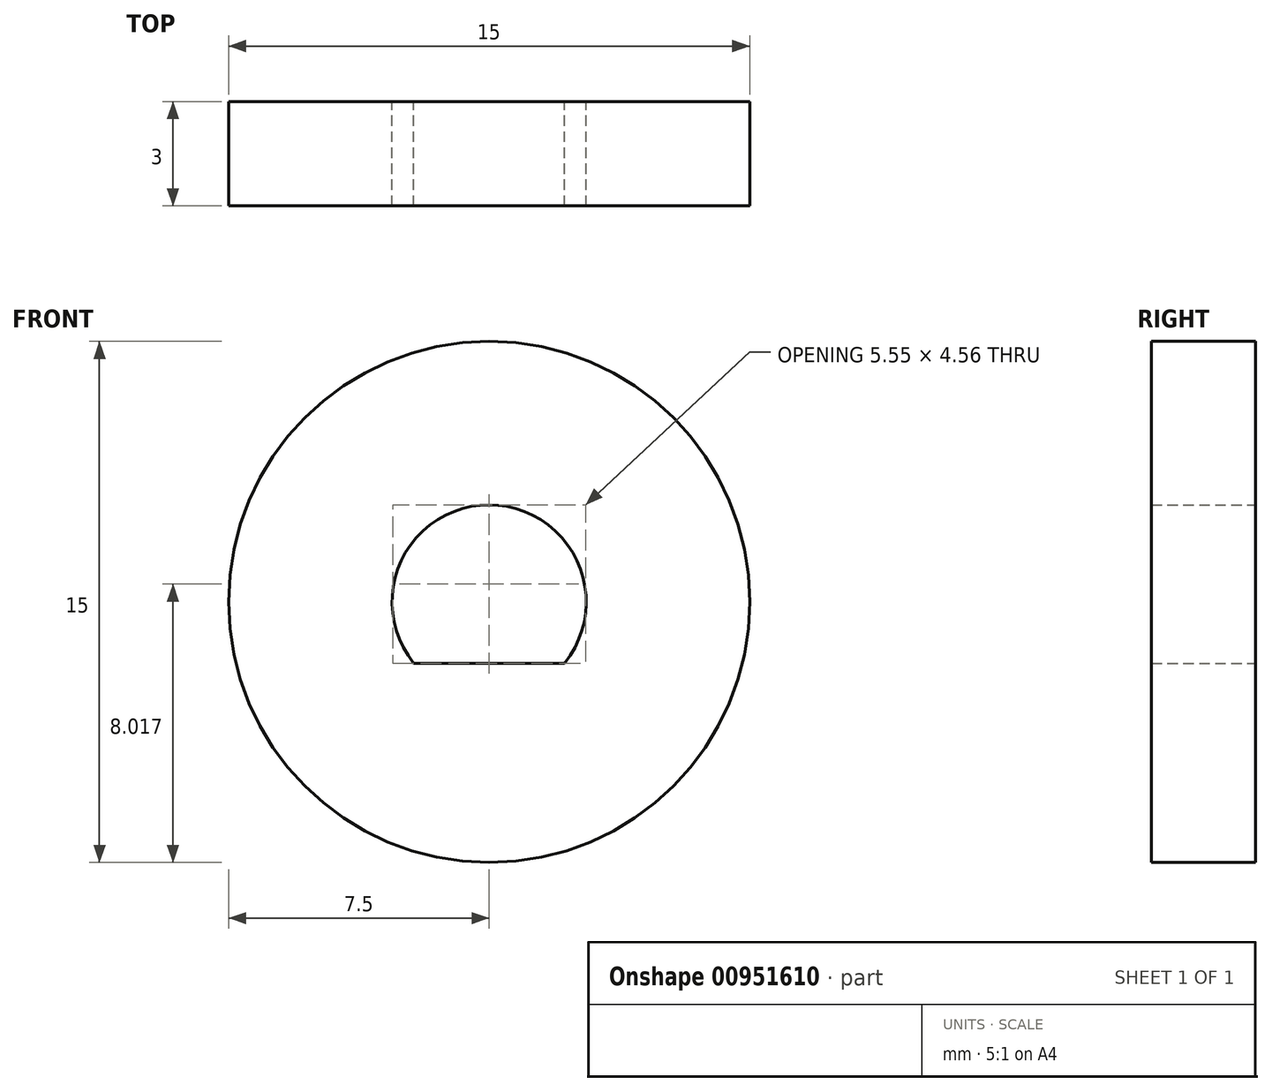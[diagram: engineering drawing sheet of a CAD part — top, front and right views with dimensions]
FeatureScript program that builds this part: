
annotation { "Feature Type Name" : "Feature", "Feature Type Description" : "" }
export const myFeature = defineFeature(function(context is Context, id is Id, definition is map)
    precondition{}
    {
        {
            var Q0;
            Q0=qCreatedBy(makeId("Front.planeOp"),FACE);
            var sketch = newSketch(context, id + "F0", { "sketchPlane" : qUnion([Q0])});
            skCircle(sketch, "E0", {"center": v(0, 0) * mm, "radius": 7.5 * mm});
            skPoint(sketch, "E1", {"position": v(-2.17, -1.76) * mm});
            skPoint(sketch, "E2", {"position": v(2.17, -1.76) * mm});
            skLineSegment(sketch, "E3", {"start": v(-2.17, -1.76) * mm, "end": v(2.17, -1.76) * mm});
            skArc(sketch, "E4", {"start": v(2.17, -1.76) * mm, "mid": v(0, 2.8) * mm, "end": v(-2.17, -1.76) * mm});
            skLineSegment(sketch, "E5", {"start": v(0, 2.8) * mm, "end": v(0, -1.76) * mm, "construction": true});
            skCircle(sketch, "E6", {"center": v(0, 0) * mm, "radius": 2.8 * mm, "construction": true});
            skLineSegment(sketch, "E7", {"start": v(0, -1.76) * mm, "end": v(0, -2.8) * mm, "construction": true});
            skSolve(sketch);
        }
        {
            var Q0;
            Q0=qSketchRegion(id+"F0",true);
            extrude(context, id + "F1", {"entities" : qUnion([Q0]), "depth" : 3 * mm, "offsetDistance" : 25 * mm});
        }
    });
